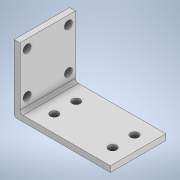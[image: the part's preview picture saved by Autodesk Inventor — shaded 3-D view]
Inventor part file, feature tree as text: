
AUTODESK INVENTOR PART (.ipt)
format: ipt  version: 2021 (Build 250183000, 183)  size: 144,896 bytes
history: native  units: mm
features: sketch x3, hole x2, projected_geometry x2, extrude x1
ambient origin geometry x8: Origin, YZ Plane, XZ Plane, XY Plane, X Axis, Y Axis, Z Axis, Center Point
bodies: Solid1 (feature_tree)
feature tree (8):
  extrude  "Extrusion1"  Depth=4.0mm
  hole  "Hole1"  [1 undecoded]
  hole  "Hole2"  [1 undecoded]
  sketch  "Sketch1"  dims[d0=2.0mm d1=4.0mm]
  sketch  "Sketch2"  dims[d2=4.0mm d3=40.0mm]
  projected_geometry  "Projected Loop1"
  sketch  "Sketch3"  dims[d5=60.0mm d6=38.0mm d7=0.0mm d10=5.5mm d11=6.0mm d12=8.0mm d13=4.0mm d14=90.0deg d15=8.0mm d16=20.594885mm d17=40.0mm d18=28.284271mm d19=28.284271mm d20=15.0mm d21=40.0mm d22=5.5mm d23=6.0mm d24=8.0mm d25=4.0mm d26=90.0deg d27=8.0mm d28=20.594885mm]
  projected_geometry  "Projected Loop2"
note: 2 required parameter values undecoded (feature->parameter linkage not recoverable at this tier; creation-order binding heuristic only, values carry confidence <= 0.55)
